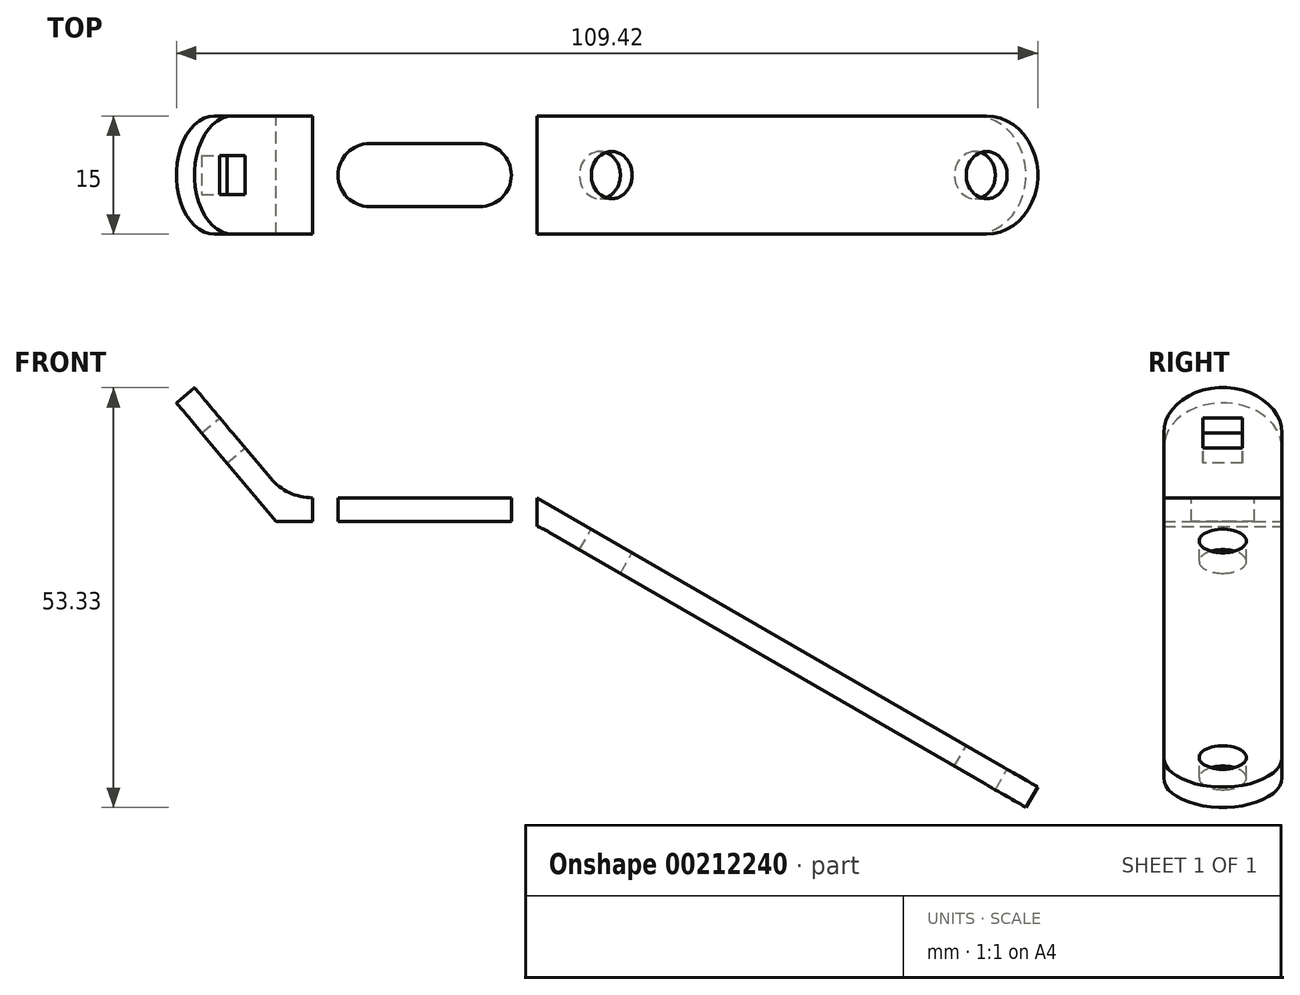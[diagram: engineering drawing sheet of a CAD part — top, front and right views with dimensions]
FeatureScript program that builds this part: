
annotation { "Feature Type Name" : "Feature", "Feature Type Description" : "" }
export const myFeature = defineFeature(function(context is Context, id is Id, definition is map)
    precondition{}
    {
        {
            var Q0;
            Q0=qCreatedBy(makeId("Front.planeOp"),FACE);
            var sketch = newSketch(context, id + "F0", { "sketchPlane" : qUnion([Q0])});
            skLineSegment(sketch, "E0", {"start": v(-15, 7) * mm, "end": v(-5.36, -4.5) * mm});
            skLineSegment(sketch, "E1", {"start": v(0, -7) * mm, "end": v(28.48, -7) * mm});
            skLineSegment(sketch, "E2", {"start": v(28.48, -7) * mm, "end": v(92.12, -43.74) * mm});
            skArc(sketch, "E3", {"start": v(0, -7) * mm, "mid": v(-2.96, -6.34) * mm, "end": v(-5.36, -4.5) * mm});
            skLineSegment(sketch, "E4.0", {"start": v(30, -11.34) * mm, "end": v(90.62, -46.34) * mm});
            skLineSegment(sketch, "E4.1", {"start": v(-4.66, -10) * mm, "end": v(25, -10) * mm});
            skLineSegment(sketch, "E4.2", {"start": v(-17.3, 5.06) * mm, "end": v(-4.66, -10) * mm});
            skArc(sketch, "E5", {"start": v(30, -11.34) * mm, "mid": v(27.59, -10.34) * mm, "end": v(25, -10) * mm});
            skLineSegment(sketch, "E6", {"start": v(-17.3, 5.06) * mm, "end": v(-15, 7) * mm});
            skLineSegment(sketch, "E7", {"start": v(90.62, -46.34) * mm, "end": v(92.12, -43.74) * mm});
            skSolve(sketch);
        }
        {
            var Q0;
            Q0 = qSketchRegion(id + "F0", true);
            extrude(context, id + "F1", {"entities" : qUnion([Q0]), "endBound" : BoundingType.SYMMETRIC, "depth" : 15 * mm});
        }
        {
            var Q0;
            Q0=makeQuery(id+"F1.opExtrude","SWEPT_FACE",FACE,{"disambiguationData":[OSD([sQuery(id+"F0.wireOp",EDGE,"E0")])]});
            var sketch = newSketch(context, id + "F2", { "sketchPlane" : qUnion([Q0])});
            skArc(sketch, "E8", {"start": v(7.5, 7.5) * mm, "mid": v(0, 15) * mm, "end": v(-7.5, 7.5) * mm});
            skPoint(sketch, "E8.centerSnap0", {"position": v(7.5, 7.5) * mm});
            skLineSegment(sketch, "E9.bottom", {"start": v(2.5, 10) * mm, "end": v(-2.5, 10) * mm});
            skLineSegment(sketch, "E9.top", {"start": v(2.5, 5) * mm, "end": v(-2.5, 5) * mm});
            skLineSegment(sketch, "E9.left", {"start": v(2.5, 10) * mm, "end": v(2.5, 5) * mm});
            skLineSegment(sketch, "E9.right", {"start": v(-2.5, 10) * mm, "end": v(-2.5, 5) * mm});
            skLineSegment(sketch, "E10.0", {"start": v(-7.5, 15) * mm, "end": v(7.5, 15) * mm});
            skLineSegment(sketch, "E10.1", {"start": v(7.5, 15) * mm, "end": v(7.5, 7.5) * mm});
            skLineSegment(sketch, "E10.2", {"start": v(-7.5, 15) * mm, "end": v(-7.5, 7.5) * mm});
            skPoint(sketch, "E11.orphan", {"position": v(-7.5, 0) * mm});
            skPoint(sketch, "E12.orphan", {"position": v(7.5, 0) * mm});
            skSolve(sketch);
        }
        {
            var Q0;
            {var subQ0=sQuery(id+"F2.wireOp",EDGE,"E10.2");Q0=makeQuery(id+"F2.imprint","IMPRINT",FACE,{"disambiguationData":[TD([[makeQuery(id+"F2.imprint","IMPRINT",EDGE,{"derivedFrom":subQ0}),1.0]])]});}
            var Q1;
            Q1=makeQuery(id+"F2.imprint","IMPRINT",FACE,{"disambiguationData":[TD([[makeQuery(id+"F2.imprint","IMPRINT",EDGE,{"derivedFrom":sQuery(id+"F2.wireOp",EDGE,"E9.bottom")}),1.0]])]});
            var Q2;
            {var subQ0=sQuery(id+"F2.wireOp",EDGE,"E10.1");Q2=makeQuery(id+"F2.imprint","IMPRINT",FACE,{"disambiguationData":[TD([[makeQuery(id+"F2.imprint","IMPRINT",EDGE,{"derivedFrom":subQ0}),-1.0]])]});}
            extrude(context, id + "F3", {"entities" : qUnion([Q0, Q1, Q2]), "operationType" : NewBodyOperationType.REMOVE, "endBound" : BoundingType.THROUGH_ALL, "oppositeDirection" : true, "depth" : 25 * mm});
        }
        {
            var Q0;
            Q0=makeQuery(id+"F1.opExtrude","SWEPT_FACE",FACE,{"disambiguationData":[OSD([sQuery(id+"F0.wireOp",EDGE,"E1")])]});
            var sketch = newSketch(context, id + "F4", { "sketchPlane" : qUnion([Q0])});
            skLineSegment(sketch, "E13", {"start": v(7.24, 0) * mm, "end": v(21.24, 0) * mm});
            skLineSegment(sketch, "E14", {"start": v(14.24, -7.5) * mm, "end": v(14.24, 7.5) * mm, "construction": true});
            skArc(sketch, "E15.0.startCap", {"start": v(7.24, -4) * mm, "mid": v(3.24, 0) * mm, "end": v(7.24, 4) * mm});
            skArc(sketch, "E15.0.endCap", {"start": v(21.24, 4) * mm, "mid": v(25.24, 0) * mm, "end": v(21.24, -4) * mm});
            skLineSegment(sketch, "E15.0.left", {"start": v(7.24, 4) * mm, "end": v(21.24, 4) * mm});
            skLineSegment(sketch, "E15.0.right", {"start": v(7.24, -4) * mm, "end": v(21.24, -4) * mm});
            skSolve(sketch);
        }
        {
            var Q0;
            Q0=makeQuery(id+"F4.imprint","IMPRINT",FACE,{"disambiguationData":[TD([[makeQuery(id+"F4.imprint","IMPRINT",EDGE,{"derivedFrom":sQuery(id+"F4.wireOp",EDGE,"E15.0.startCap")}),-1.0]])]});
            extrude(context, id + "F5", {"entities" : qUnion([Q0]), "operationType" : NewBodyOperationType.REMOVE, "endBound" : BoundingType.THROUGH_ALL, "oppositeDirection" : true, "depth" : 25 * mm});
        }
        {
            var Q0;
            Q0=makeQuery(id+"F1.opExtrude","SWEPT_FACE",FACE,{"disambiguationData":[OSD([sQuery(id+"F0.wireOp",EDGE,"E2")])]});
            var sketch = newSketch(context, id + "F6", { "sketchPlane" : qUnion([Q0])});
            skArc(sketch, "E16", {"start": v(94.15, -7.5) * mm, "mid": v(101.65, 0) * mm, "end": v(94.15, 7.5) * mm});
            skPoint(sketch, "E16.centerSnap0", {"position": v(101.65, 0) * mm});
            skCircle(sketch, "E17", {"center": v(94.15, 0) * mm, "radius": 3 * mm});
            skCircle(sketch, "E18", {"center": v(39.15, 0) * mm, "radius": 3 * mm});
            skLineSegment(sketch, "E19.0", {"start": v(94.15, -7.5) * mm, "end": v(101.65, -7.5) * mm});
            skLineSegment(sketch, "E19.1", {"start": v(94.15, 7.5) * mm, "end": v(101.65, 7.5) * mm});
            skLineSegment(sketch, "E19.2", {"start": v(101.65, -7.5) * mm, "end": v(101.65, 7.5) * mm});
            skPoint(sketch, "E20.orphan", {"position": v(28.17, -7.5) * mm});
            skPoint(sketch, "E21.orphan", {"position": v(28.17, 7.5) * mm});
            skSolve(sketch);
        }
        {
            var Q0;
            Q0=makeQuery(id+"F6.imprint","IMPRINT",FACE,{"disambiguationData":[TD([[makeQuery(id+"F6.imprint","IMPRINT",EDGE,{"derivedFrom":sQuery(id+"F6.wireOp",EDGE,"E18")}),1.0]])]});
            var Q1;
            Q1=makeQuery(id+"F6.imprint","IMPRINT",FACE,{"disambiguationData":[TD([[makeQuery(id+"F6.imprint","IMPRINT",EDGE,{"derivedFrom":sQuery(id+"F6.wireOp",EDGE,"E17")}),1.0]])]});
            var Q2;
            {var subQ0=sQuery(id+"F6.wireOp",EDGE,"E19.1");Q2=makeQuery(id+"F6.imprint","IMPRINT",FACE,{"disambiguationData":[TD([[makeQuery(id+"F6.imprint","IMPRINT",EDGE,{"derivedFrom":subQ0}),-1.0]])]});}
            var Q3;
            {var subQ0=sQuery(id+"F6.wireOp",EDGE,"E19.0");Q3=makeQuery(id+"F6.imprint","IMPRINT",FACE,{"disambiguationData":[TD([[makeQuery(id+"F6.imprint","IMPRINT",EDGE,{"derivedFrom":subQ0}),1.0]])]});}
            extrude(context, id + "F7", {"entities" : qUnion([Q0, Q1, Q2, Q3]), "operationType" : NewBodyOperationType.REMOVE, "endBound" : BoundingType.THROUGH_ALL, "oppositeDirection" : true, "depth" : 25 * mm});
        }
    });
